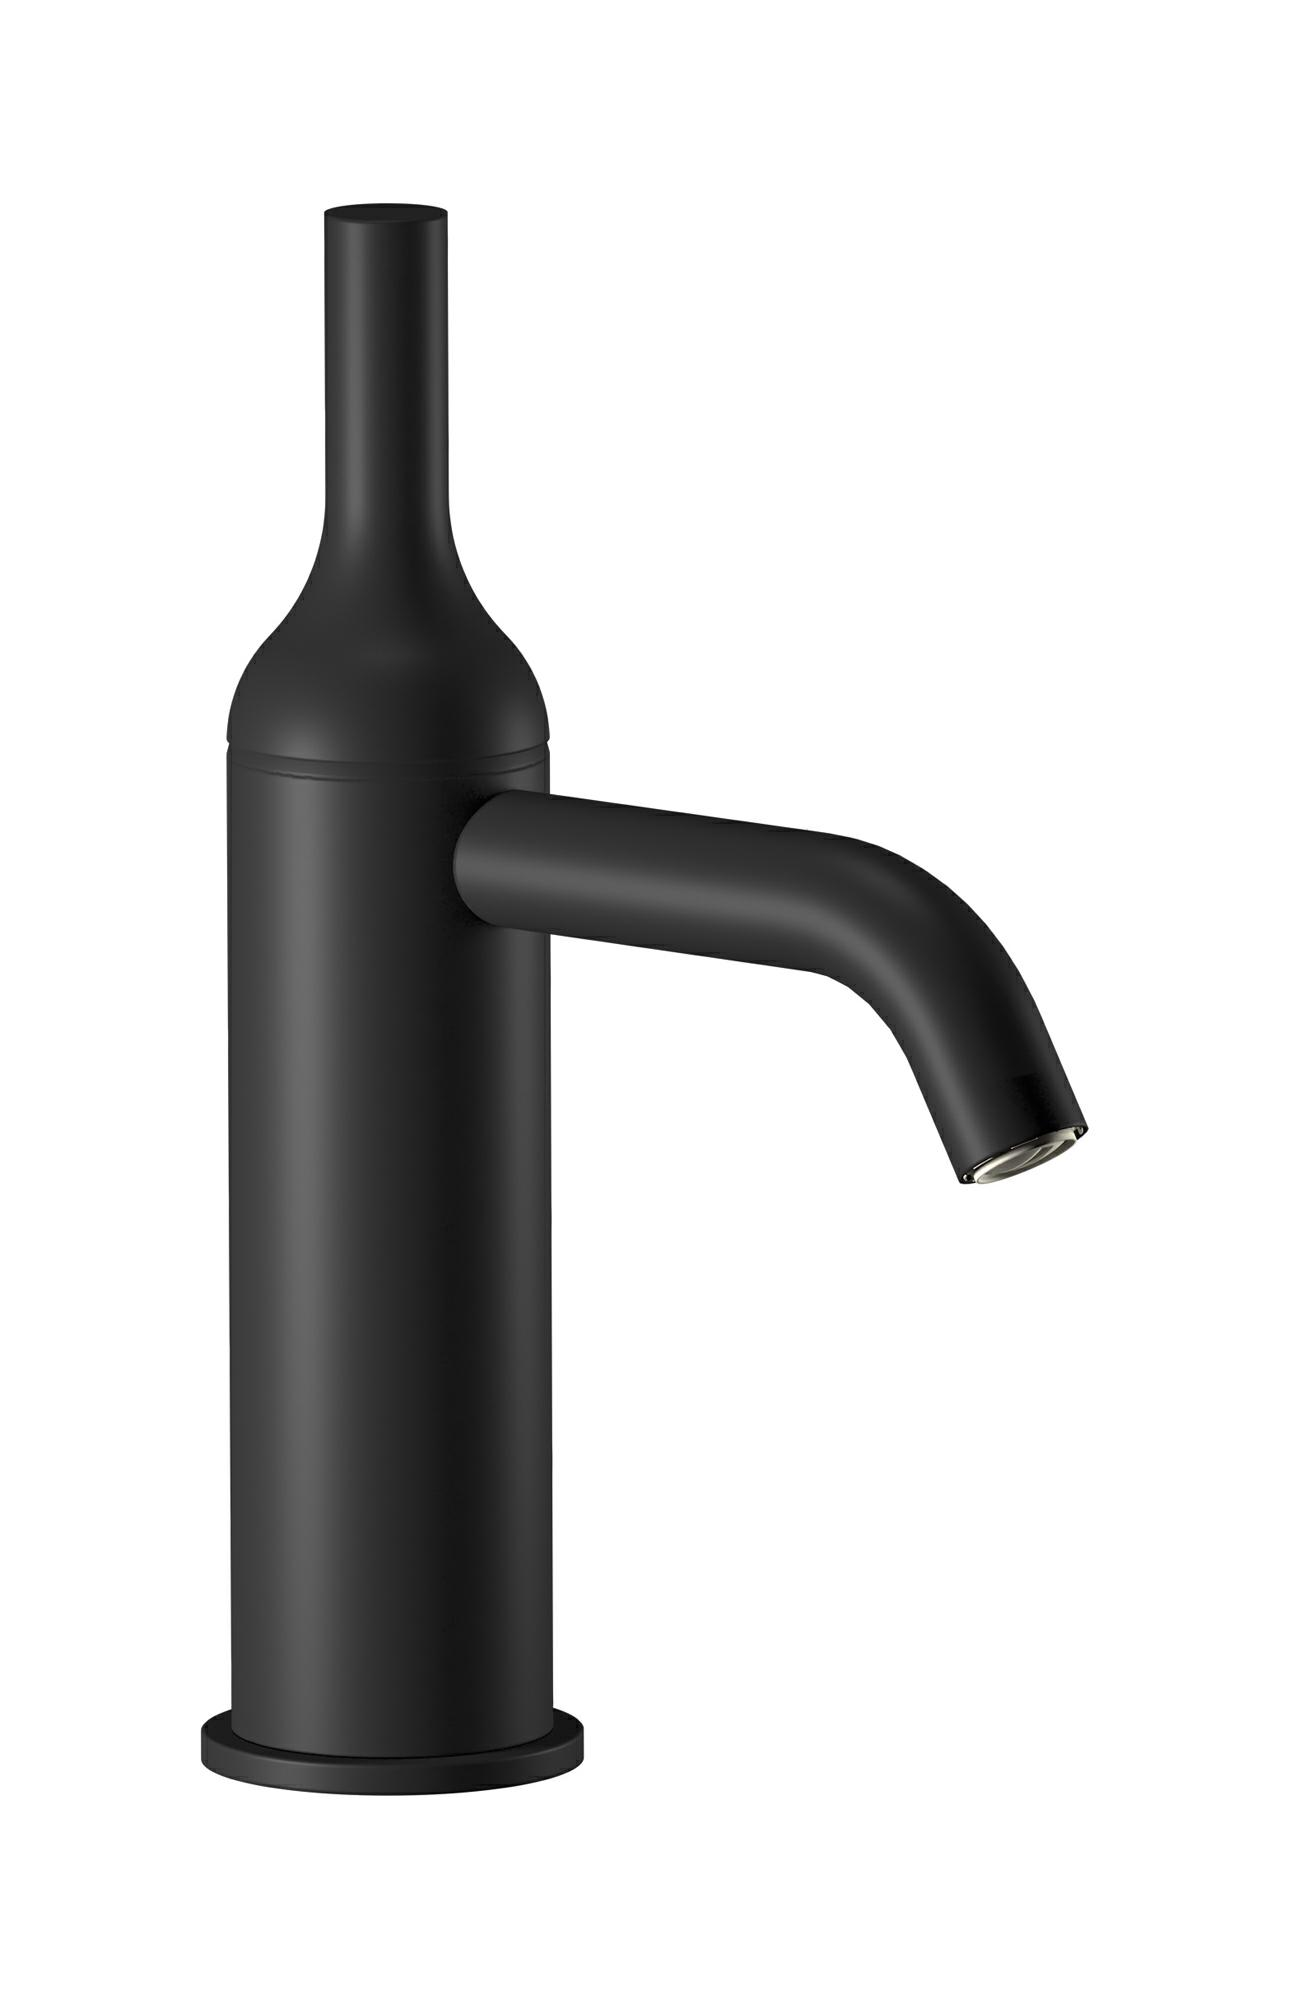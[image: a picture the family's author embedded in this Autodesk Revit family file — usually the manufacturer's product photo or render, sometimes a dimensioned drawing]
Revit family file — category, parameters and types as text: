
# Revit family: BI200
name_source: partatom
category: Apparecchi idraulici
units: mm (PartAtom-declared; Revit-internal decimal feet)

## family parameters
Basato su piano di lavoro = No
Condiviso = No
Mantieni orientamento annotazione = No
Numero OmniClass = 23.45.55.17
Punto di calcolo locali = No
Quota connettore circolare = Usa diametro
Sempre verticale = Sì
Taglio con vuoti quando caricato = No
Tipo di parte = Normale
Titolo OmniClass = Mixing Faucets

## types (4) — shared parameters
Cold water inlet = 10 mm  [stored 0.0328084 ft]
Commenti sul tipo = Monohole washbasin mixer complete with drain
Connessione CW = No
Connessione HW = No
Connessione di scarico = No
Connessione di ventilazione = No
Descrizione = Monohole washbasin mixer complete with drain
Hot water flow = 0,0 L/s
Hot water inlet = 10 mm  [stored 0.0328084 ft]
Produttore = IB Rubinetterie S.p.A.
URL = https://www.weareib.it
zero-valued in all types: Prospetto di default

## per-type parameters (varying)
| type | Finishes surface | Immagine tipo | Modello |
| Chrome | IB_Chrome | BI200CC.jpg | BI200CC |
| Brushed nickel | IB_Brushed nickel | BI200SS.jpg | BI200SS |
| Matt white | IB_matt white | BI200BO.jpg | BI200BO |
| Matt black | IB_matt black | BI200NP.jpg | BI200NP |

note: [stored X ft] marks values corroborated as IEEE doubles in the binary element streams (Revit-internal decimal feet)
